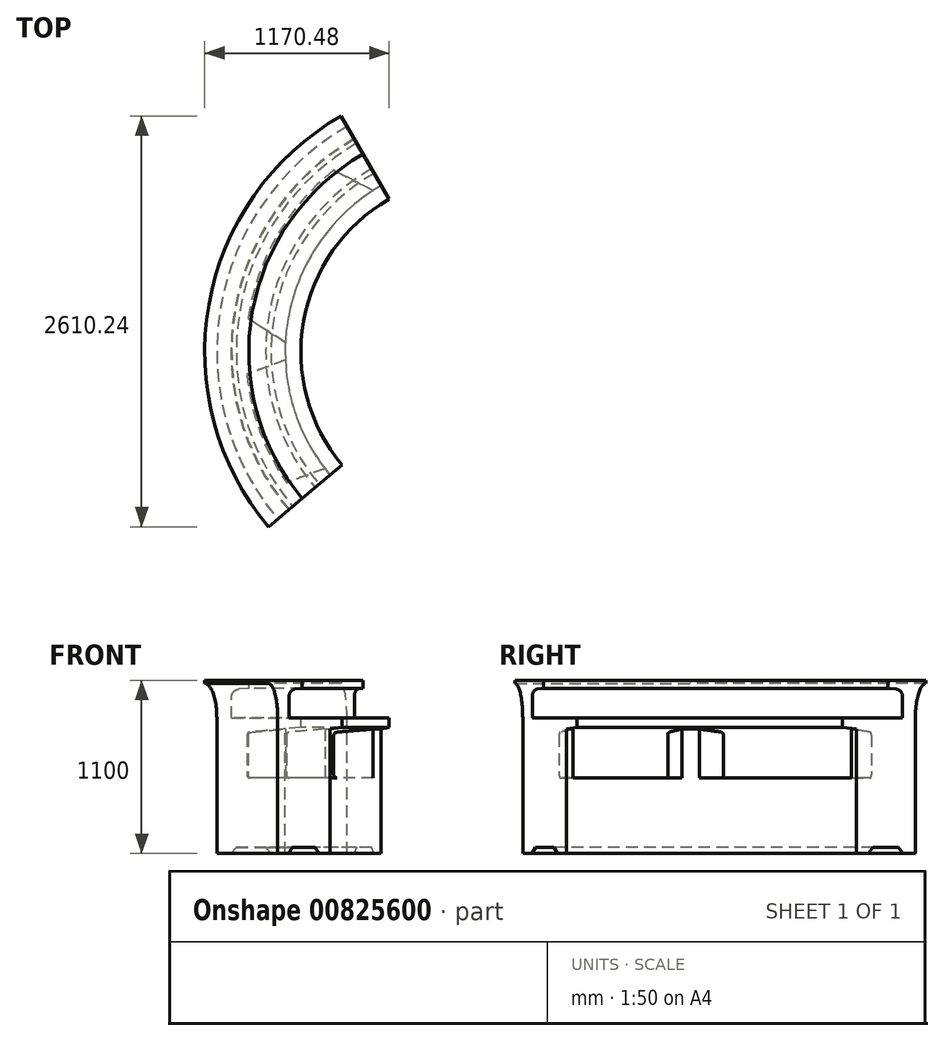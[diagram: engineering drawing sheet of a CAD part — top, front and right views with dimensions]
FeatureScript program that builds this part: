
annotation { "Feature Type Name" : "Feature", "Feature Type Description" : "" }
export const myFeature = defineFeature(function(context is Context, id is Id, definition is map)
    precondition{}
    {
        {
            var Q0;
            Q0=qCreatedBy(makeId("Front.planeOp"),FACE);
            var sketch = newSketch(context, id + "F0", { "sketchPlane" : qUnion([Q0])});
            skLineSegment(sketch, "E0", {"start": v(77, 0) * mm, "end": v(77, 860) * mm});
            skEllipticalArc(sketch, "E1", {});
            skPoint(sketch, "E2", {"position": v(0, 1080) * mm});
            skLineSegment(sketch, "E3", {"start": v(610.96, 860) * mm, "end": v(170.96, 860) * mm});
            skLineSegment(sketch, "E4", {"start": v(170.96, 860) * mm, "end": v(170.96, 994.64) * mm});
            skLineSegment(sketch, "E5", {"start": v(216.6, 1044.45) * mm, "end": v(280, 1050) * mm});
            skLineSegment(sketch, "E6", {"start": v(280, 1050) * mm, "end": v(280, 1100) * mm});
            skPoint(sketch, "E7.visualSharp", {"position": v(170.96, 1040.46) * mm});
            skArc(sketch, "E7.filletArc", {"start": v(216.6, 1044.45) * mm, "mid": v(184.1, 1028.42) * mm, "end": v(170.96, 994.64) * mm});
            skLineSegment(sketch, "E8", {"start": v(610.96, 800) * mm, "end": v(279.22, 770.98) * mm});
            skLineSegment(sketch, "E9", {"start": v(260.96, 751.05) * mm, "end": v(260.96, 500) * mm});
            skLineSegment(sketch, "E10", {"start": v(280.96, 480) * mm, "end": v(510.96, 480) * mm});
            skLineSegment(sketch, "E11", {"start": v(510.96, 480) * mm, "end": v(510.96, 0) * mm});
            skLineSegment(sketch, "E12", {"start": v(510.96, 0) * mm, "end": v(420.96, 0) * mm});
            skLineSegment(sketch, "E13", {"start": v(420.96, 0) * mm, "end": v(387.4, 40) * mm});
            skLineSegment(sketch, "E14", {"start": v(387.4, 40) * mm, "end": v(200.56, 40) * mm});
            skLineSegment(sketch, "E15", {"start": v(200.56, 40) * mm, "end": v(167, 0) * mm});
            skLineSegment(sketch, "E16", {"start": v(167, 0) * mm, "end": v(77, 0) * mm});
            skPoint(sketch, "E17.visualSharp", {"position": v(260.96, 769.38) * mm});
            skArc(sketch, "E17.filletArc", {"start": v(279.22, 770.98) * mm, "mid": v(266.22, 764.56) * mm, "end": v(260.96, 751.05) * mm});
            skPoint(sketch, "E18.visualSharp", {"position": v(260.96, 480) * mm});
            skArc(sketch, "E18.filletArc", {"start": v(260.96, 500) * mm, "mid": v(266.82, 485.86) * mm, "end": v(280.96, 480) * mm});
            skLineSegment(sketch, "E19", {"start": v(610.96, 860) * mm, "end": v(610.96, 800) * mm});
            skLineSegment(sketch, "E20", {"start": v(280, 1100) * mm, "end": v(0, 1100) * mm});
            skLineSegment(sketch, "E21", {"start": v(0, 1100) * mm, "end": v(0, 1080) * mm});
            const initialGuessF0  = {"E1": [0, 0.86, 0, 1, 0.22, 0.077, 4.71238898038469, 0]};
            skSetInitialGuess(sketch, initialGuessF0);
            skSolve(sketch);
        }
        {
            var Q0;
            Q0=qCreatedBy(makeId("Top.planeOp"),FACE);
            var sketch = newSketch(context, id + "F1", { "sketchPlane" : qUnion([Q0])});
            skCircle(sketch, "E22", {"center": v(1730, 0) * mm, "radius": 1730 * mm});
            skLineSegment(sketch, "E23", {"start": v(0, 0) * mm, "end": v(885.12, 1509.66) * mm, "construction": true});
            skLineSegment(sketch, "E24", {"start": v(1730, 0) * mm, "end": v(885.12, 1509.66) * mm, "construction": true});
            skLineSegment(sketch, "E25", {"start": v(1730, 0) * mm, "end": v(0, 0) * mm, "construction": true});
            skLineSegment(sketch, "E26", {"start": v(0, 0) * mm, "end": v(0.72, 50) * mm, "construction": true});
            skLineSegment(sketch, "E27", {"start": v(0.72, 50) * mm, "end": v(1730, 0) * mm, "construction": true});
            skLineSegment(sketch, "E28", {"start": v(0, 0) * mm, "end": v(289.02, -957.32) * mm, "construction": true});
            skLineSegment(sketch, "E29", {"start": v(289.02, -957.32) * mm, "end": v(1730, 0) * mm, "construction": true});
            skLineSegment(sketch, "E30", {"start": v(1730, 0) * mm, "end": v(416.18, -1125.52) * mm, "construction": true});
            skSolve(sketch);
        }
        {
            var Q0;
            Q0=makeQuery(id+"F0.imprint","IMPRINT",FACE,{"disambiguationData":[TD([[makeQuery(id+"F0.imprint","IMPRINT",EDGE,{"derivedFrom":sQuery(id+"F0.wireOp",EDGE,"E0")}),-1.0]])]});
            var Q1;
            Q1=sQuery(id+"F1.wireOp",EDGE,"E22");
            revolve(context, id + "F2", {"surfaceOperationType" : NewSurfaceOperationType.NEW, "entities" : qUnion([Q0]), "axis" : qUnion([Q1]), "revolveType" : RevolveType.ONE_DIRECTION, "oppositeDirection" : true, "angle" : 60 * degree});
        }
        {
            var Q0;
            Q0=makeQuery(id+"F2.opRevolve","CAP_FACE",FACE,{"disambiguationData":[OSD([sQuery(id+"F0.wireOp",EDGE,"E0"),sQuery(id+"F0.wireOp",EDGE,"E1"),sQuery(id+"F0.wireOp",EDGE,"E3"),sQuery(id+"F0.wireOp",EDGE,"E4"),sQuery(id+"F0.wireOp",EDGE,"E5"),sQuery(id+"F0.wireOp",EDGE,"E6"),sQuery(id+"F0.wireOp",EDGE,"E7.filletArc"),sQuery(id+"F0.wireOp",EDGE,"E8"),sQuery(id+"F0.wireOp",EDGE,"E9"),sQuery(id+"F0.wireOp",EDGE,"E10"),sQuery(id+"F0.wireOp",EDGE,"E11"),sQuery(id+"F0.wireOp",EDGE,"E12"),sQuery(id+"F0.wireOp",EDGE,"E13"),sQuery(id+"F0.wireOp",EDGE,"E14"),sQuery(id+"F0.wireOp",EDGE,"E15"),sQuery(id+"F0.wireOp",EDGE,"E16"),sQuery(id+"F0.wireOp",EDGE,"E17.filletArc"),sQuery(id+"F0.wireOp",EDGE,"E18.filletArc"),sQuery(id+"F0.wireOp",EDGE,"E19"),sQuery(id+"F0.wireOp",EDGE,"E20"),sQuery(id+"F0.wireOp",EDGE,"E21")])],"isStart":true});
            var sketch = newSketch(context, id + "F3", { "sketchPlane" : qUnion([Q0])});
            skLineSegment(sketch, "E31.1", {"start": v(77, 0) * mm, "end": v(77, 860) * mm});
            skLineSegment(sketch, "E32", {"start": v(77, 860) * mm, "end": v(610.96, 860) * mm});
            skLineSegment(sketch, "E33", {"start": v(610.96, 860) * mm, "end": v(610.96, 800) * mm});
            skLineSegment(sketch, "E34", {"start": v(610.96, 800) * mm, "end": v(510.96, 791.25) * mm});
            skPoint(sketch, "E31.0.end.orphan", {"position": v(0, 1080) * mm});
            skLineSegment(sketch, "E35", {"start": v(77, 0) * mm, "end": v(510.96, 0) * mm});
            skLineSegment(sketch, "E36", {"start": v(510.96, 0) * mm, "end": v(510.96, 791.25) * mm});
            skSolve(sketch);
        }
        {
            var Q0;
            Q0=makeQuery(id+"F2.opRevolve","SWEPT_FACE",FACE,{"disambiguationData":[OSD([sQuery(id+"F0.wireOp",EDGE,"E10")])]});
            var sketch = newSketch(context, id + "F4", { "sketchPlane" : qUnion([Q0])});
            skLineSegment(sketch, "E37", {"start": v(510.96, 0) * mm, "end": v(1120.48, 1055.72) * mm, "construction": true});
            skLineSegment(sketch, "E38", {"start": v(1095.48, 1012.42) * mm, "end": v(833.43, 1163.71) * mm, "construction": true});
            skLineSegment(sketch, "E39", {"start": v(535.96, 43.3) * mm, "end": v(273.9, 194.6) * mm, "construction": true});
            skLineSegment(sketch, "E40", {"start": v(512.37, 58.62) * mm, "end": v(276.33, 211.91) * mm});
            skLineSegment(sketch, "E41", {"start": v(1070.42, 1025.19) * mm, "end": v(819.64, 1152.96) * mm});
            skPoint(sketch, "E42.orphan", {"position": v(995.48, 1272.23) * mm});
            skPoint(sketch, "E43.orphan", {"position": v(260.96, 0) * mm});
            skArc(sketch, "E44.0", {"start": v(995.48, 1272.23) * mm, "mid": v(905.4, 1215.78) * mm, "end": v(819.64, 1152.96) * mm});
            skArc(sketch, "E45.0", {"start": v(1120.48, 1055.72) * mm, "mid": v(1095.27, 1040.75) * mm, "end": v(1070.42, 1025.19) * mm});
            skArc(sketch, "E46.trimOffspring", {"start": v(276.33, 211.91) * mm, "mid": v(264.8, 106.23) * mm, "end": v(260.96, 0) * mm});
            skArc(sketch, "E47.trimOffspring", {"start": v(512.37, 58.62) * mm, "mid": v(511.31, 29.32) * mm, "end": v(510.96, 0) * mm});
            skLineSegment(sketch, "E48", {"start": v(260.96, 0) * mm, "end": v(510.96, 0) * mm});
            skLineSegment(sketch, "E49", {"start": v(995.48, 1272.23) * mm, "end": v(1120.48, 1055.72) * mm});
            skSolve(sketch);
        }
        {
            var Q0;
            Q0 = qSketchRegion(id + "F4", true);
            var Q1;
            Q1=sQuery(id+"F3.wireOp",VERTEX,"E34.end");
            extrude(context, id + "F5", {"entities" : qUnion([Q0]), "operationType" : NewBodyOperationType.ADD, "endBound" : BoundingType.UP_TO_VERTEX, "depth" : 25 * mm, "endBoundEntityVertex" : qUnion([Q1]), "offsetDistance" : 25 * mm});
        }
        {
            var Q0;
            Q0 = qSketchRegion(id + "F0", true);
            var Q1;
            Q1=sQuery(id+"F1.wireOp",EDGE,"E22");
            revolve(context, id + "F6", {"surfaceOperationType" : NewSurfaceOperationType.NEW, "entities" : qUnion([Q0]), "axis" : qUnion([Q1]), "revolveType" : RevolveType.ONE_DIRECTION, "angle" : 40 * degree});
        }
        {
            var Q0;
            Q0=makeQuery(id+"F6.opRevolve","SWEPT_FACE",FACE,{"disambiguationData":[OSD([sQuery(id+"F0.wireOp",EDGE,"E10")])]});
            var sketch = newSketch(context, id + "F7", { "sketchPlane" : qUnion([Q0])});
            skArc(sketch, "E50.0", {"start": v(604.65, -944.28) * mm, "mid": v(560.37, -888.84) * mm, "end": v(518.81, -831.32) * mm});
            skArc(sketch, "E51.0", {"start": v(796.16, -783.58) * mm, "mid": v(779.4, -763.17) * mm, "end": v(763.1, -742.4) * mm});
            skLineSegment(sketch, "E52", {"start": v(510.96, 0) * mm, "end": v(796.16, -783.58) * mm, "construction": true});
            skLineSegment(sketch, "E53", {"start": v(512.1, -52.8) * mm, "end": v(267.81, -141.7) * mm});
            skLineSegment(sketch, "E54", {"start": v(763.1, -742.4) * mm, "end": v(518.81, -831.32) * mm});
            skPoint(sketch, "E55.orphan", {"position": v(528.06, -46.98) * mm});
            skPoint(sketch, "E56.orphan", {"position": v(779.06, -736.6) * mm});
            skArc(sketch, "E57.trimOffspring", {"start": v(512.1, -52.8) * mm, "mid": v(511.25, -26.4) * mm, "end": v(510.96, 0) * mm});
            skArc(sketch, "E58.trimOffspring", {"start": v(267.81, -141.7) * mm, "mid": v(262.67, -70.94) * mm, "end": v(260.96, 0) * mm});
            skLineSegment(sketch, "E59", {"start": v(260.96, 0) * mm, "end": v(510.96, 0) * mm});
            skLineSegment(sketch, "E60", {"start": v(604.65, -944.28) * mm, "end": v(796.16, -783.58) * mm});
            skSolve(sketch);
        }
        {
            var Q0;
            Q0 = qSketchRegion(id + "F7", true);
            var Q1;
            Q1=makeQuery(id+"F5.opExtrude","CAP_VERTEX",VERTEX,{"disambiguationData":[OSD([sQuery(id+"F0.wireOp",EDGE,"E10"),sQuery(id+"F0.wireOp",EDGE,"E11"),sQuery(id+"F4.wireOp",EDGE,"E41"),sQuery(id+"F4.wireOp",EDGE,"E45.0"),dummyQuery(id+"F5.vertexPlane.planeOp",FACE)])],"isStart":false});
            extrude(context, id + "F8", {"entities" : qUnion([Q0]), "operationType" : NewBodyOperationType.ADD, "endBound" : BoundingType.UP_TO_VERTEX, "depth" : 25 * mm, "endBoundEntityVertex" : qUnion([Q1]), "offsetDistance" : 25 * mm});
        }
    });
